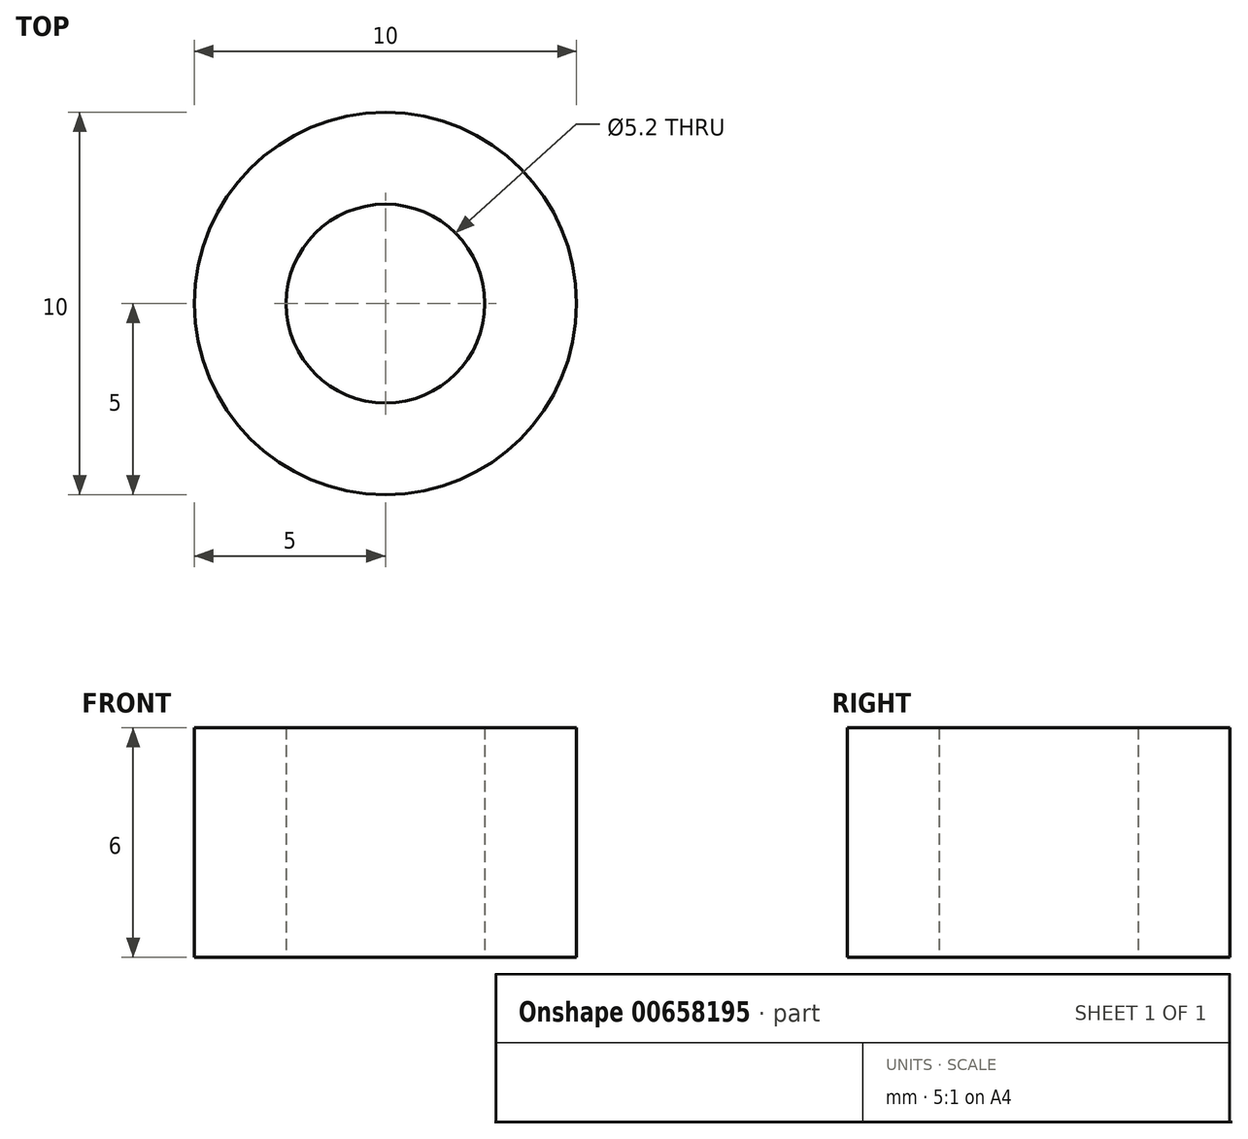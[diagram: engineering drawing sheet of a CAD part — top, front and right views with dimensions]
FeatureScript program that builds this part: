
annotation { "Feature Type Name" : "Feature", "Feature Type Description" : "" }
export const myFeature = defineFeature(function(context is Context, id is Id, definition is map)
    precondition{}
    {
        {
            var Q0;
            Q0=qCreatedBy(makeId("Top.planeOp"),FACE);
            var sketch = newSketch(context, id + "F0", { "sketchPlane" : qUnion([Q0])});
            skCircle(sketch, "E0", {"center": v(0, 0) * mm, "radius": 2.6 * mm});
            skCircle(sketch, "E1", {"center": v(0, 0) * mm, "radius": 5 * mm});
            skSolve(sketch);
        }
        {
            var Q0;
            Q0=makeQuery(id+"F0.imprint","IMPRINT",FACE,{"disambiguationData":[TD([[makeQuery(id+"F0.imprint","IMPRINT",EDGE,{"derivedFrom":sQuery(id+"F0.wireOp",EDGE,"E0")}),-1.0]])]});
            extrude(context, id + "F1", {"entities" : qUnion([Q0]), "depth" : 6 * mm, "offsetDistance" : 25.4 * mm});
        }
    });
